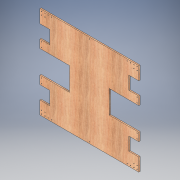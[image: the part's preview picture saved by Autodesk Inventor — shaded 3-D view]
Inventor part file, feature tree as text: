
AUTODESK INVENTOR PART (.ipt)
format: ipt  version: 2018 (Build 220112000, 112)  size: 253,952 bytes
history: native  units: in
note: dims shown in document units (in); Inventor stores cm internally (conversion verified against a paired STEP export)
features: extrude x3, sketch x3
ambient origin geometry x8: Origin, YZ Plane, XZ Plane, XY Plane, X Axis, Y Axis, Z Axis, Center Point
bodies: Solid1 (feature_tree)
feature tree (6):
  extrude  "Extrusion1"  Depth=4.0in
  extrude  "Extrusion2"  Depth=4.0in
  extrude  "Extrusion4"  Depth=9.0in
  sketch  "Sketch1"  dims[d0=30.0in d1=4.0in]
  sketch  "Sketch2"  dims[d2=3.0in d3=4.0in]
  sketch  "Sketch4"  dims[d4=2.5in d5=9.0in d7=3.5in d8=0.375in d9=0.0in d10=0.5in d11=0.5in d12=1.0in d13=1.0in d14=1.0in d16=0.2in d17=0.5in d18=0.5in d19=0.5in d20=0.375in d21=0.0in d29=1.0in d30=1.0in d32=0.5in d33=1.0in d34=0.0in]
